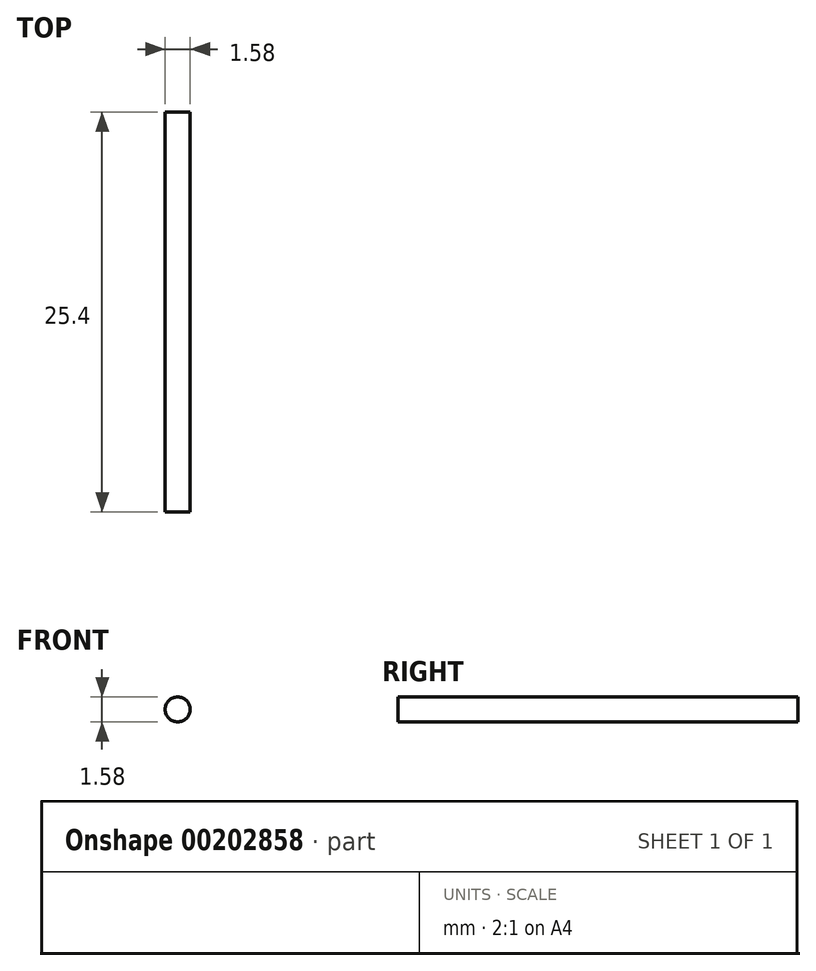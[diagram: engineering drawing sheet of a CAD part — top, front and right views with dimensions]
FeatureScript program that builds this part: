
annotation { "Feature Type Name" : "Feature", "Feature Type Description" : "" }
export const myFeature = defineFeature(function(context is Context, id is Id, definition is map)
    precondition{}
    {
        {
            var Q0;
            Q0=qCreatedBy(makeId("Front.planeOp"),FACE);
            var sketch = newSketch(context, id + "F0", { "sketchPlane" : qUnion([Q0])});
            skCircle(sketch, "E0", {"center": v(0, 0) * mm, "radius": 0.8 * mm});
            skSolve(sketch);
        }
        {
            var Q0;
            Q0 = qSketchRegion(id + "F0", true);
            extrude(context, id + "F1", {"entities" : qUnion([Q0]), "endBound" : BoundingType.SYMMETRIC, "depth" : 25.4 * mm});
        }
    });
